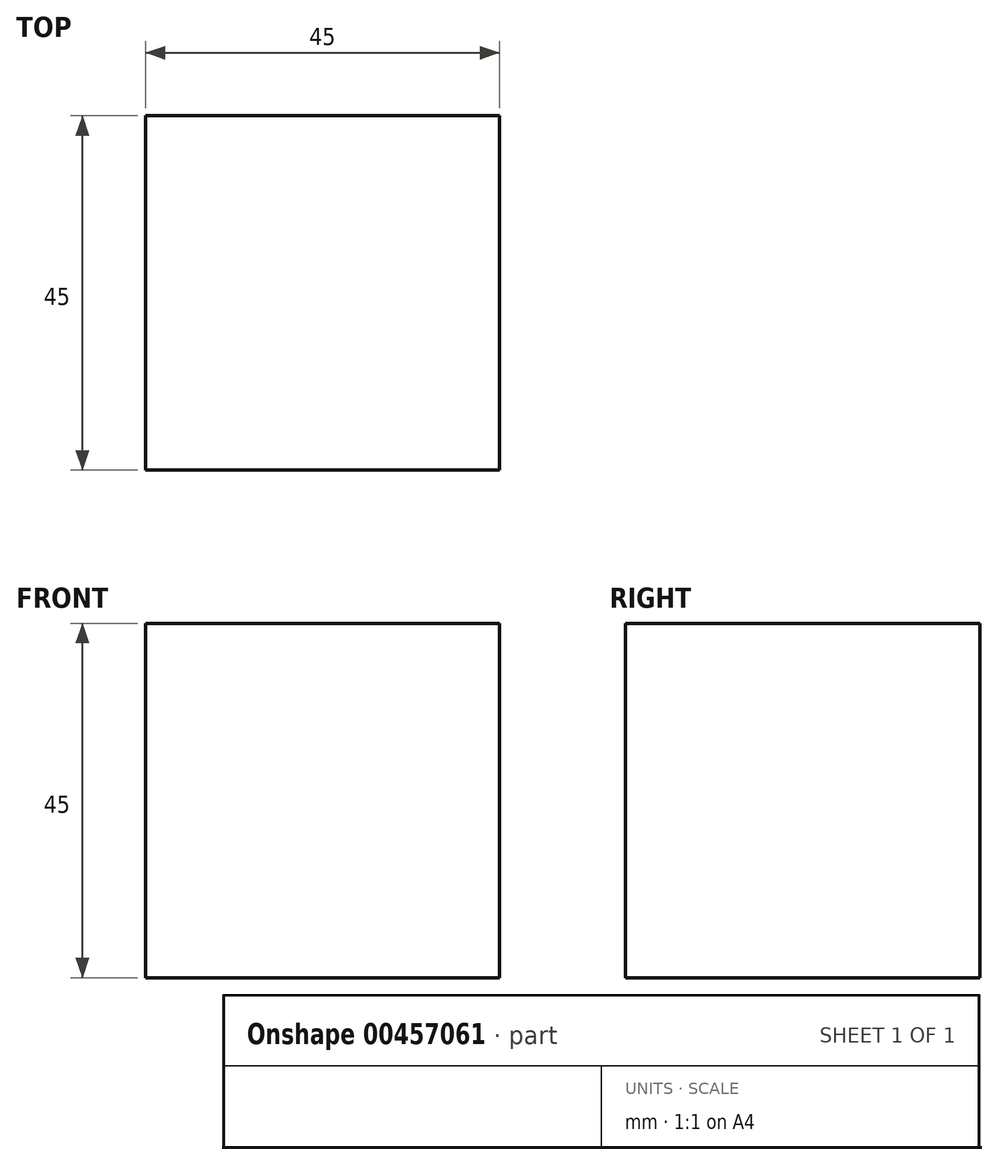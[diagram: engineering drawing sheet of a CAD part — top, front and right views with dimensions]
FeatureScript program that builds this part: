
annotation { "Feature Type Name" : "Feature", "Feature Type Description" : "" }
export const myFeature = defineFeature(function(context is Context, id is Id, definition is map)
    precondition{}
    {
        {
            var Q0;
            Q0=qCreatedBy(makeId("Front.planeOp"),FACE);
            var sketch = newSketch(context, id + "F0", { "sketchPlane" : qUnion([Q0])});
            skLineSegment(sketch, "E0.bottom", {"start": v(22.5, 22.5) * mm, "end": v(-22.5, 22.5) * mm});
            skLineSegment(sketch, "E0.top", {"start": v(22.5, -22.5) * mm, "end": v(-22.5, -22.5) * mm});
            skLineSegment(sketch, "E0.left", {"start": v(22.5, 22.5) * mm, "end": v(22.5, -22.5) * mm});
            skLineSegment(sketch, "E0.right", {"start": v(-22.5, 22.5) * mm, "end": v(-22.5, -22.5) * mm});
            skPoint(sketch, "E0.middle", {"position": v(0, 0) * mm});
            skSolve(sketch);
        }
        {
            var Q0;
            Q0=makeQuery(id+"F0.imprint","IMPRINT",FACE,{"disambiguationData":[TD([[makeQuery(id+"F0.imprint","IMPRINT",EDGE,{"derivedFrom":sQuery(id+"F0.wireOp",EDGE,"E0.bottom")}),1.0]])]});
            extrude(context, id + "F1", {"entities" : qUnion([Q0]), "depth" : 45 * mm});
        }
    });
